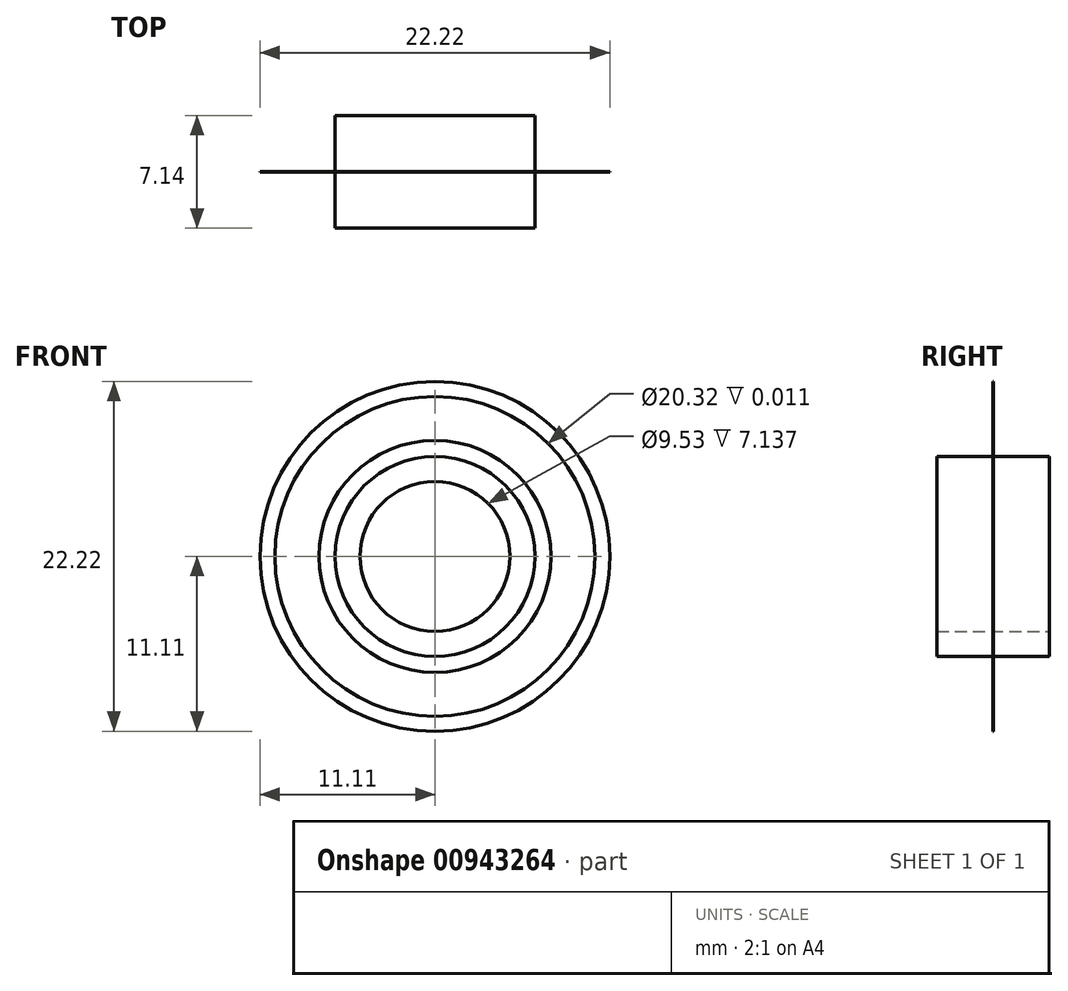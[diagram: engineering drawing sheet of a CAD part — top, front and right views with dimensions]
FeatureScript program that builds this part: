
annotation { "Feature Type Name" : "Feature", "Feature Type Description" : "" }
export const myFeature = defineFeature(function(context is Context, id is Id, definition is map)
    precondition{}
    {
        {
            var Q0;
            Q0=qCreatedBy(makeId("Front.planeOp"),FACE);
            var sketch = newSketch(context, id + "F0", { "sketchPlane" : qUnion([Q0])});
            skCircle(sketch, "E0", {"center": v(0, 0) * mm, "radius": 11.11 * mm});
            skCircle(sketch, "E1", {"center": v(0, 0) * mm, "radius": 6.35 * mm});
            skSolve(sketch);
        }
        {
            var Q0;
            Q0=qSketchRegion(id+"F0",true);
            extrude(context, id + "F1", {"entities" : qUnion([Q0]), "endBound" : BoundingType.SYMMETRIC, "depth" : 9 / 812.8 * mm, "offsetDistance" : 25.4 * mm});
        }
        {
            var Q0;
            Q0=makeQuery(id+"F1.opExtrude","CAP_FACE",FACE,{"disambiguationData":[OSD([sQuery(id+"F0.wireOp",EDGE,"E0"),sQuery(id+"F0.wireOp",EDGE,"E1")])],"isStart":false});
            var sketch = newSketch(context, id + "F2", { "sketchPlane" : qUnion([Q0])});
            skCircle(sketch, "E2", {"center": v(0, 0) * mm, "radius": 7.37 * mm});
            skCircle(sketch, "E3", {"center": v(0, 0) * mm, "radius": 10.16 * mm});
            skSolve(sketch);
        }
        {
            var Q0;
            Q0=qSketchRegion(id+"F2",true);
            extrude(context, id + "F3", {"entities" : qUnion([Q0]), "operationType" : NewBodyOperationType.REMOVE, "oppositeDirection" : true, "depth" : 0.38 * mm, "offsetDistance" : 25.4 * mm});
        }
        {
            var Q0;
            Q0=qCreatedBy(makeId("Front.planeOp"),FACE);
            var sketch = newSketch(context, id + "F4", { "sketchPlane" : qUnion([Q0])});
            skCircle(sketch, "E4", {"center": v(0, 0) * mm, "radius": 6.35 * mm});
            skCircle(sketch, "E5", {"center": v(0, 0) * mm, "radius": 4.76 * mm});
            skSolve(sketch);
        }
        {
            var Q0;
            Q0 = qSketchRegion(id + "F4", true);
            extrude(context, id + "F5", {"entities" : qUnion([Q0]), "operationType" : NewBodyOperationType.ADD, "endBound" : BoundingType.SYMMETRIC, "depth" : 7.14 * mm, "offsetDistance" : 25.4 * mm});
        }
    });
